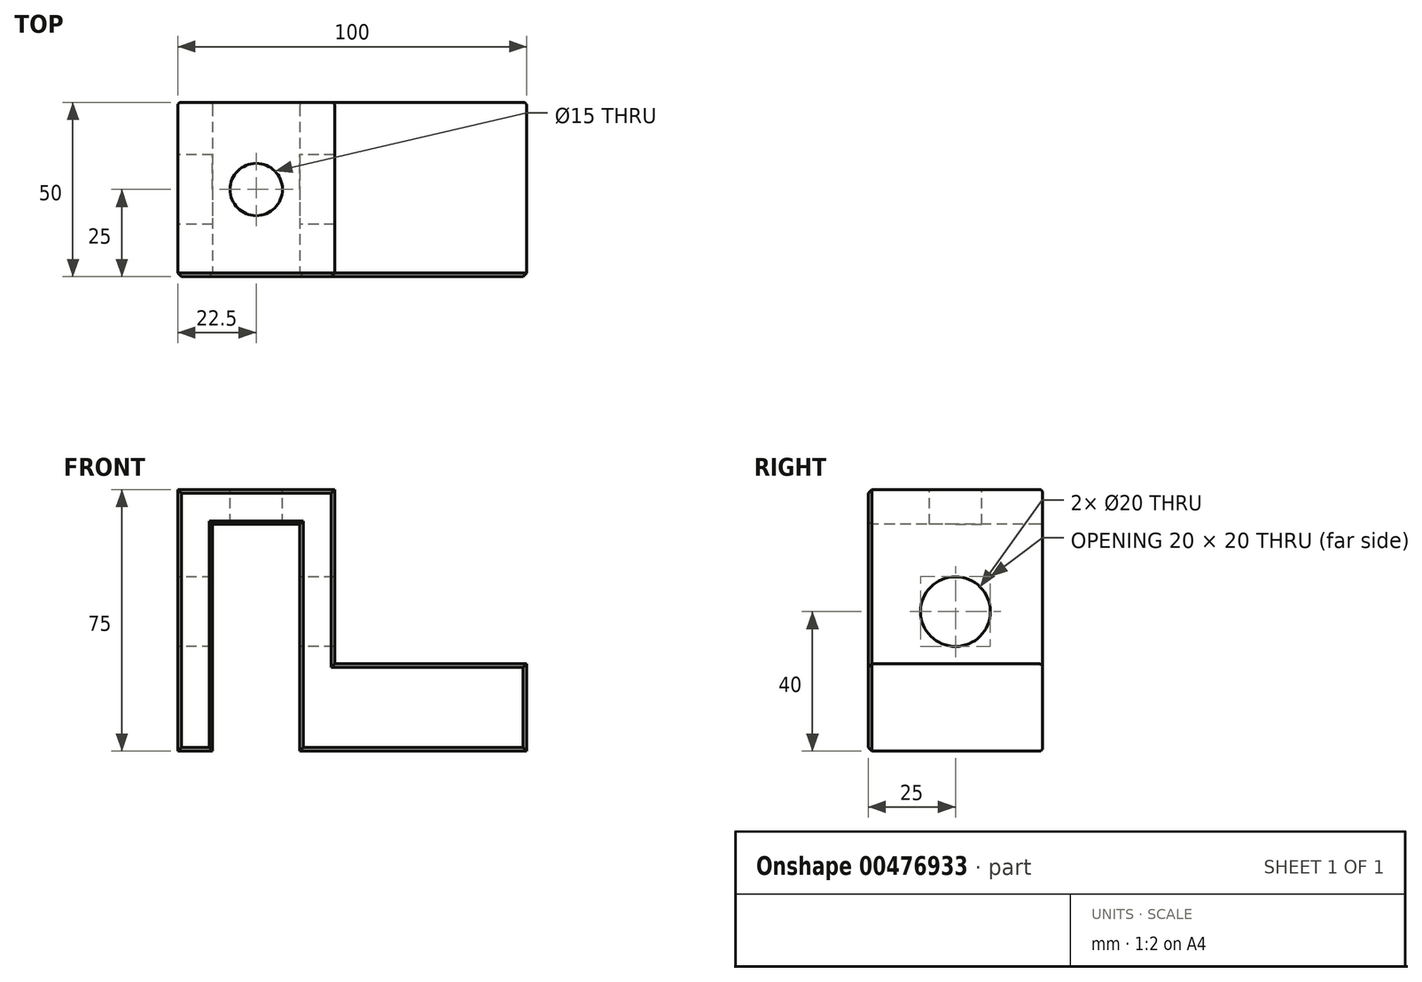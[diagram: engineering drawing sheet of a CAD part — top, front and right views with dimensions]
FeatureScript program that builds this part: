
annotation { "Feature Type Name" : "Feature", "Feature Type Description" : "" }
export const myFeature = defineFeature(function(context is Context, id is Id, definition is map)
    precondition{}
    {
        {
            var Q0;
            Q0=qCreatedBy(makeId("Top.planeOp"),FACE);
            var sketch = newSketch(context, id + "F0", { "sketchPlane" : qUnion([Q0])});
            skLineSegment(sketch, "E0.bottom", {"start": v(0, 0) * mm, "end": v(100, 0) * mm});
            skLineSegment(sketch, "E0.top", {"start": v(0, 50) * mm, "end": v(100, 50) * mm});
            skLineSegment(sketch, "E0.left", {"start": v(0, 0) * mm, "end": v(0, 50) * mm});
            skLineSegment(sketch, "E0.right", {"start": v(100, 0) * mm, "end": v(100, 50) * mm});
            skSolve(sketch);
        }
        {
            var Q0;
            Q0 = qSketchRegion(id + "F0", true);
            extrude(context, id + "F1", {"entities" : qUnion([Q0]), "depth" : 25 * mm});
        }
        {
            var Q0;
            Q0=makeQuery(id+"F1.opExtrude","CAP_FACE",FACE,{"disambiguationData":[OSD([sQuery(id+"F0.wireOp",EDGE,"E0.bottom"),sQuery(id+"F0.wireOp",EDGE,"E0.top"),sQuery(id+"F0.wireOp",EDGE,"E0.left"),sQuery(id+"F0.wireOp",EDGE,"E0.right")])],"isStart":false});
            var sketch = newSketch(context, id + "F2", { "sketchPlane" : qUnion([Q0])});
            skLineSegment(sketch, "E1.bottom", {"start": v(0, 0) * mm, "end": v(45, 0) * mm});
            skLineSegment(sketch, "E1.top", {"start": v(0, 50) * mm, "end": v(45, 50) * mm});
            skLineSegment(sketch, "E1.left", {"start": v(0, 0) * mm, "end": v(0, 50) * mm});
            skLineSegment(sketch, "E1.right", {"start": v(45, 0) * mm, "end": v(45, 50) * mm});
            skSolve(sketch);
        }
        {
            var Q0;
            Q0 = qSketchRegion(id + "F2", true);
            extrude(context, id + "F3", {"entities" : qUnion([Q0]), "operationType" : NewBodyOperationType.ADD, "depth" : 50 * mm});
        }
        {
            var Q0;
            Q0=makeQuery(id+"F3.boolean.opBoolean","MERGE",FACE,{"derivedFrom":[makeQuery(id+"F1.opExtrude","SWEPT_FACE",FACE,{"disambiguationData":[OSD([sQuery(id+"F0.wireOp",EDGE,"E0.bottom")])]}),makeQuery(id+"F3.opExtrude","SWEPT_FACE",FACE,{"disambiguationData":[OSD([sQuery(id+"F2.wireOp",EDGE,"E1.bottom")])]})]});
            var sketch = newSketch(context, id + "F4", { "sketchPlane" : qUnion([Q0])});
            skLineSegment(sketch, "E2.bottom", {"start": v(10, 0) * mm, "end": v(35, 0) * mm});
            skLineSegment(sketch, "E2.top", {"start": v(10, 65) * mm, "end": v(35, 65) * mm});
            skLineSegment(sketch, "E2.left", {"start": v(10, 0) * mm, "end": v(10, 65) * mm});
            skLineSegment(sketch, "E2.right", {"start": v(35, 0) * mm, "end": v(35, 65) * mm});
            skSolve(sketch);
        }
        {
            var Q0;
            Q0 = qSketchRegion(id + "F4", true);
            extrude(context, id + "F5", {"entities" : qUnion([Q0]), "operationType" : NewBodyOperationType.REMOVE, "endBound" : BoundingType.THROUGH_ALL, "oppositeDirection" : true, "depth" : 25 * mm});
        }
        {
            var Q0;
            Q0=makeQuery(id+"F3.boolean.opBoolean","MERGE",FACE,{"derivedFrom":[makeQuery(id+"F1.opExtrude","SWEPT_FACE",FACE,{"disambiguationData":[OSD([sQuery(id+"F0.wireOp",EDGE,"E0.left")])]}),makeQuery(id+"F3.opExtrude","SWEPT_FACE",FACE,{"disambiguationData":[OSD([sQuery(id+"F2.wireOp",EDGE,"E1.left")])]})]});
            var sketch = newSketch(context, id + "F6", { "sketchPlane" : qUnion([Q0])});
            skCircle(sketch, "E3", {"center": v(-25, 40) * mm, "radius": 10 * mm});
            skSolve(sketch);
        }
        {
            var Q0;
            Q0 = qSketchRegion(id + "F6", true);
            extrude(context, id + "F7", {"entities" : qUnion([Q0]), "operationType" : NewBodyOperationType.REMOVE, "endBound" : BoundingType.THROUGH_ALL, "oppositeDirection" : true, "depth" : 25 * mm});
        }
        {
            var Q0;
            Q0=makeQuery(id+"F3.opExtrude","CAP_FACE",FACE,{"disambiguationData":[OSD([sQuery(id+"F2.wireOp",EDGE,"E1.bottom"),sQuery(id+"F2.wireOp",EDGE,"E1.top"),sQuery(id+"F2.wireOp",EDGE,"E1.left"),sQuery(id+"F2.wireOp",EDGE,"E1.right")])],"isStart":false});
            var sketch = newSketch(context, id + "F8", { "sketchPlane" : qUnion([Q0])});
            skLineSegment(sketch, "E4", {"start": v(45, 50) * mm, "end": v(0, 0) * mm, "construction": true});
            skLineSegment(sketch, "E5", {"start": v(0, 0) * mm, "end": v(0, 50) * mm, "construction": true});
            skLineSegment(sketch, "E6", {"start": v(0, 50) * mm, "end": v(45, 0) * mm, "construction": true});
            skCircle(sketch, "E7", {"center": v(22.5, 25) * mm, "radius": 7.5 * mm});
            skSolve(sketch);
        }
        {
            var Q0;
            Q0=makeQuery(id+"F8.imprint","IMPRINT",FACE,{"disambiguationData":[TD([[makeQuery(id+"F8.imprint","IMPRINT",EDGE,{"derivedFrom":sQuery(id+"F8.wireOp",EDGE,"E7")}),1.0]])]});
            extrude(context, id + "F9", {"entities" : qUnion([Q0]), "operationType" : NewBodyOperationType.REMOVE, "endBound" : BoundingType.UP_TO_NEXT, "oppositeDirection" : true, "depth" : 25 * mm});
        }
        {
            var Q0;
            Q0=makeQuery(id+"F3.boolean.opBoolean","MERGE",EDGE,{"derivedFrom":[makeQuery(id+"F1.opExtrude","SWEPT_EDGE",EDGE,{"disambiguationData":[OSD([sQuery(id+"F0.wireOp",EDGE,"E0.bottom"),sQuery(id+"F0.wireOp",EDGE,"E0.left")])]}),makeQuery(id+"F3.opExtrude","SWEPT_EDGE",EDGE,{"disambiguationData":[OSD([sQuery(id+"F2.wireOp",EDGE,"E1.bottom"),sQuery(id+"F2.wireOp",EDGE,"E1.left")])]})]});
            var Q1;
            Q1=makeQuery(id+"F5.boolean.opBoolean","COPY",EDGE,{"derivedFrom":makeQuery(id+"F5.opExtrude","CAP_EDGE",EDGE,{"disambiguationData":[OSD([sQuery(id+"F4.wireOp",EDGE,"E2.right")])],"isStart":true})});
            var Q2;
            Q2=makeQuery(id+"F5.boolean.opBoolean","COPY",EDGE,{"derivedFrom":makeQuery(id+"F5.opExtrude","CAP_EDGE",EDGE,{"disambiguationData":[OSD([sQuery(id+"F4.wireOp",EDGE,"E2.top")])],"isStart":true})});
            var Q3;
            {var subQ0=sQuery(id+"F0.wireOp",EDGE,"E0.left");var subQ1=sQuery(id+"F0.wireOp",EDGE,"E0.bottom");Q3=makeQuery(id+"F5.boolean.opBoolean","SPLIT",EDGE,{"disambiguationData":[TD([makeQuery(id+"F1.opExtrude","SWEPT_FACE",FACE,{"disambiguationData":[OSD([subQ0])]})])],"derivedFrom":makeQuery(id+"F1.opExtrude","CAP_EDGE",EDGE,{"disambiguationData":[OSD([subQ1])],"isStart":true})});}
            var Q4;
            Q4=makeQuery(id+"F3.boolean.opBoolean","MERGE",FACE,{"derivedFrom":[makeQuery(id+"F1.opExtrude","SWEPT_FACE",FACE,{"disambiguationData":[OSD([sQuery(id+"F0.wireOp",EDGE,"E0.bottom")])]}),makeQuery(id+"F3.opExtrude","SWEPT_FACE",FACE,{"disambiguationData":[OSD([sQuery(id+"F2.wireOp",EDGE,"E1.bottom")])]})]});
            chamfer(context, id + "F10", {"entities" : qUnion([Q0, Q1, Q2, Q3, Q4]), "width" : 1 * mm, "tangentPropagation" : true});
        }
        {
            var Q0;
            Q0=makeQuery(id+"F1.opExtrude","CAP_EDGE",EDGE,{"disambiguationData":[OSD([sQuery(id+"F0.wireOp",EDGE,"E0.top")])],"isStart":false});
            var Q1;
            Q1=makeQuery(id+"F3.opExtrude","SWEPT_EDGE",EDGE,{"disambiguationData":[OSD([sQuery(id+"F0.wireOp",EDGE,"E0.top"),sQuery(id+"F2.wireOp",EDGE,"E1.top"),sQuery(id+"F2.wireOp",EDGE,"E1.right")])]});
            var Q2;
            Q2=makeQuery(id+"F3.opExtrude","CAP_EDGE",EDGE,{"disambiguationData":[OSD([sQuery(id+"F2.wireOp",EDGE,"E1.top")])],"isStart":false});
            var Q3;
            Q3=makeQuery(id+"F3.boolean.opBoolean","MERGE",EDGE,{"derivedFrom":[makeQuery(id+"F1.opExtrude","SWEPT_EDGE",EDGE,{"disambiguationData":[OSD([sQuery(id+"F0.wireOp",EDGE,"E0.top"),sQuery(id+"F0.wireOp",EDGE,"E0.left")])]}),makeQuery(id+"F3.opExtrude","SWEPT_EDGE",EDGE,{"disambiguationData":[OSD([sQuery(id+"F2.wireOp",EDGE,"E1.top"),sQuery(id+"F2.wireOp",EDGE,"E1.left")])]})]});
            var Q4;
            Q4=makeQuery(id+"F3.boolean.opBoolean","MERGE",FACE,{"derivedFrom":[makeQuery(id+"F1.opExtrude","SWEPT_FACE",FACE,{"disambiguationData":[OSD([sQuery(id+"F0.wireOp",EDGE,"E0.top")])]}),makeQuery(id+"F3.opExtrude","SWEPT_FACE",FACE,{"disambiguationData":[OSD([sQuery(id+"F2.wireOp",EDGE,"E1.top")])]})]});
            fillet(context, id + "F11", {"entities" : qUnion([Q0, Q1, Q2, Q3, Q4]), "radius" : 1 * mm, "tangentPropagation" : true, "allowEdgeOverflow" : false});
        }
    });
